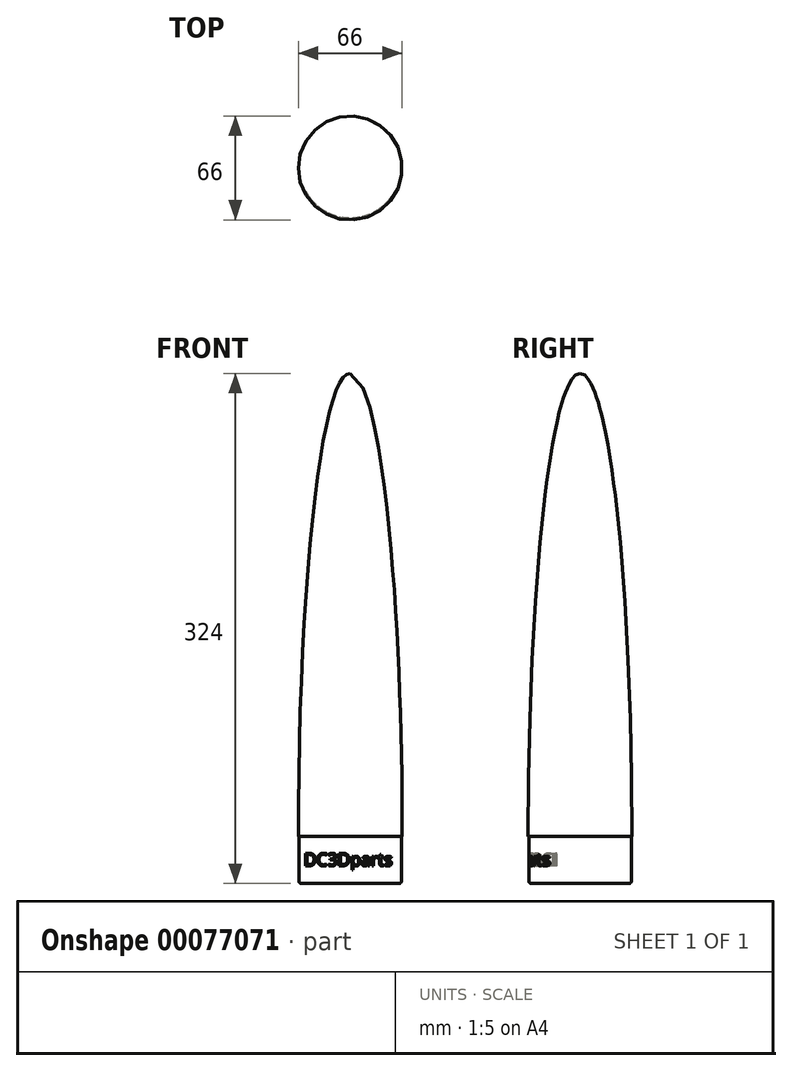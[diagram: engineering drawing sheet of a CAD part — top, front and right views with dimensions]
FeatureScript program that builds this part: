
annotation { "Feature Type Name" : "Feature", "Feature Type Description" : "" }
export const myFeature = defineFeature(function(context is Context, id is Id, definition is map)
    precondition{}
    {
        {
            var Q0;
            Q0=qCreatedBy(makeId("Front.planeOp"),FACE);
            var sketch = newSketch(context, id + "F0", { "sketchPlane" : qUnion([Q0])});
            skEllipticalArc(sketch, "E0", {});
            skLineSegment(sketch, "E1", {"start": v(0, 294) * mm, "end": v(0, -294) * mm, "construction": true});
            skPoint(sketch, "E1.endSnap0", {"position": v(0, 294) * mm});
            skLineSegment(sketch, "E2", {"start": v(-35.36, 0) * mm, "end": v(40.39, 0) * mm, "construction": true});
            skPoint(sketch, "E2.endSnap0", {"position": v(33, 0) * mm});
            skPoint(sketch, "E3.orphan", {"position": v(0, 67.2) * mm});
            skPoint(sketch, "E4.orphan", {"position": v(0, -68.03) * mm});
            skLineSegment(sketch, "E5", {"start": v(-33, 0) * mm, "end": v(-32.55, 0) * mm});
            skLineSegment(sketch, "E6", {"start": v(-32.55, 0) * mm, "end": v(-32.55, -30) * mm});
            skLineSegment(sketch, "E7", {"start": v(-32.55, -30) * mm, "end": v(0, -30) * mm});
            skLineSegment(sketch, "E8", {"start": v(0, -30) * mm, "end": v(0, 294) * mm});
            const initialGuessF0  = {"E0": [0, 0, 0, 1, 0.294, 0.033, 0, 1.5707963267948966]};
            skSetInitialGuess(sketch, initialGuessF0);
            skSolve(sketch);
        }
        {
            var Q0;
            Q0=makeQuery(id+"F0.imprint","IMPRINT",FACE,{"disambiguationData":[TD([[makeQuery(id+"F0.imprint","IMPRINT",EDGE,{"derivedFrom":sQuery(id+"F0.wireOp",EDGE,"E0")}),1.0]])]});
            var Q1;
            Q1=sQuery(id+"F0.wireOp",EDGE,"E1");
            revolve(context, id + "F1", {"entities" : qUnion([Q0]), "axis" : qUnion([Q1]), "revolveType" : RevolveType.FULL});
        }
        {
            var Q0;
            Q0=qCreatedBy(makeId("Front.planeOp"),FACE);
            cPlane(context, id + "F2", {"entities" : qUnion([Q0]), "cplaneType" : CPlaneType.OFFSET, "offset" : 40 * mm, "width" : 150 * mm, "height" : 150 * mm});
        }
        {
            var Q0;
            Q0=qCreatedBy(id+"F2.planeOp",FACE);
            var sketch = newSketch(context, id + "F3", { "sketchPlane" : qUnion([Q0])});
            skText(sketch, "E9", { "text": "DC3Dparts", "fontName": "OpenSans-Regular.ttf"});
            const initialGuessF3  = {"E9": [-0.02955, -0.01876, 1, 0, 0.008]};
            skSetInitialGuess(sketch, initialGuessF3);
            skSolve(sketch);
        }
        {
            var Q0;
            Q0=qCreatedBy(makeId("Front.planeOp"),FACE);
            var sketch = newSketch(context, id + "F4", { "sketchPlane" : qUnion([Q0])});
            skLineSegment(sketch, "E10.bottom", {"start": v(0, -9.12) * mm, "end": v(-32, -9.12) * mm});
            skLineSegment(sketch, "E10.top", {"start": v(0, -47.4) * mm, "end": v(-32, -47.4) * mm});
            skLineSegment(sketch, "E10.left", {"start": v(0, -9.12) * mm, "end": v(0, -47.4) * mm});
            skLineSegment(sketch, "E10.right", {"start": v(-32, -9.12) * mm, "end": v(-32, -47.4) * mm});
            skLineSegment(sketch, "E11.left", {"start": v(0, -47.4) * mm, "end": v(0, -47.4) * mm});
            skLineSegment(sketch, "E11.right", {"start": v(-32, -47.4) * mm, "end": v(-32, -47.4) * mm});
            skLineSegment(sketch, "E12.bottom", {"start": v(-32, -9.12) * mm, "end": v(-58.46, -9.12) * mm});
            skLineSegment(sketch, "E12.top", {"start": v(-32, -52.19) * mm, "end": v(-58.46, -52.19) * mm});
            skLineSegment(sketch, "E12.left", {"start": v(-32, -9.12) * mm, "end": v(-32, -52.19) * mm});
            skLineSegment(sketch, "E12.right", {"start": v(-58.46, -9.12) * mm, "end": v(-58.46, -52.19) * mm});
            skSolve(sketch);
        }
        {
            var Q0;
            Q0 = qSketchRegion(id + "F3", true);
            extrude(context, id + "F5", {"entities" : qUnion([Q0]), "oppositeDirection" : true, "depth" : 38 * mm, "offsetDistance" : 25 * mm});
        }
        {
            var Q0;
            {var subQ0=sQuery(id+"F4.wireOp",EDGE,"E10.bottom");Q0=makeQuery(id+"F4.imprint","IMPRINT",FACE,{"disambiguationData":[TD([[makeQuery(id+"F4.imprint","IMPRINT",EDGE,{"derivedFrom":subQ0}),1.0]])]});}
            var Q1;
            Q1=sQuery(id+"F4.wireOp",EDGE,"E10.left");
            revolve(context, id + "F6", {"entities" : qUnion([Q0]), "axis" : qUnion([Q1]), "revolveType" : RevolveType.FULL});
        }
        {
            var Q0;
            Q0=makeQuery(id+"F6.opRevolve","SWEPT_BODY",BODY,{"disambiguationData":[OSD([sQuery(id+"F4.wireOp",EDGE,"E10.bottom"),sQuery(id+"F4.wireOp",EDGE,"E10.left"),sQuery(id+"F4.wireOp",EDGE,"E10.top"),sQuery(id+"F4.wireOp",EDGE,"E12.left")])]});
            var Q1;
            Q1=makeQuery(id+"F5.opExtrude","SWEPT_BODY",BODY,{"disambiguationData":[OSD([sQuery(id+"F3.wireOp",EDGE,"E9.sketch_text.stroke-0"),sQuery(id+"F3.wireOp",EDGE,"E9.sketch_text.stroke-1"),sQuery(id+"F3.wireOp",EDGE,"E9.sketch_text.stroke-2"),sQuery(id+"F3.wireOp",EDGE,"E9.sketch_text.stroke-3"),sQuery(id+"F3.wireOp",EDGE,"E9.sketch_text.stroke-4"),sQuery(id+"F3.wireOp",EDGE,"E9.sketch_text.stroke-5"),sQuery(id+"F3.wireOp",EDGE,"E9.sketch_text.stroke-6"),sQuery(id+"F3.wireOp",EDGE,"E9.sketch_text.stroke-7"),sQuery(id+"F3.wireOp",EDGE,"E9.sketch_text.stroke-8"),sQuery(id+"F3.wireOp",EDGE,"E9.sketch_text.stroke-9"),sQuery(id+"F3.wireOp",EDGE,"E9.sketch_text.stroke-10"),sQuery(id+"F3.wireOp",EDGE,"E9.sketch_text.stroke-11"),sQuery(id+"F3.wireOp",EDGE,"E9.sketch_text.stroke-12"),sQuery(id+"F3.wireOp",EDGE,"E9.sketch_text.stroke-13")])]});
            var Q2;
            Q2=makeQuery(id+"F5.opExtrude","SWEPT_BODY",BODY,{"disambiguationData":[OSD([sQuery(id+"F3.wireOp",EDGE,"E9.sketch_text.stroke-14"),sQuery(id+"F3.wireOp",EDGE,"E9.sketch_text.stroke-15"),sQuery(id+"F3.wireOp",EDGE,"E9.sketch_text.stroke-16"),sQuery(id+"F3.wireOp",EDGE,"E9.sketch_text.stroke-17"),sQuery(id+"F3.wireOp",EDGE,"E9.sketch_text.stroke-18"),sQuery(id+"F3.wireOp",EDGE,"E9.sketch_text.stroke-19"),sQuery(id+"F3.wireOp",EDGE,"E9.sketch_text.stroke-20"),sQuery(id+"F3.wireOp",EDGE,"E9.sketch_text.stroke-21"),sQuery(id+"F3.wireOp",EDGE,"E9.sketch_text.stroke-22"),sQuery(id+"F3.wireOp",EDGE,"E9.sketch_text.stroke-23"),sQuery(id+"F3.wireOp",EDGE,"E9.sketch_text.stroke-24"),sQuery(id+"F3.wireOp",EDGE,"E9.sketch_text.stroke-25"),sQuery(id+"F3.wireOp",EDGE,"E9.sketch_text.stroke-26"),sQuery(id+"F3.wireOp",EDGE,"E9.sketch_text.stroke-27"),sQuery(id+"F3.wireOp",EDGE,"E9.sketch_text.stroke-28")])]});
            var Q3;
            Q3=makeQuery(id+"F5.opExtrude","SWEPT_BODY",BODY,{"disambiguationData":[OSD([sQuery(id+"F3.wireOp",EDGE,"E9.sketch_text.stroke-29"),sQuery(id+"F3.wireOp",EDGE,"E9.sketch_text.stroke-30"),sQuery(id+"F3.wireOp",EDGE,"E9.sketch_text.stroke-31"),sQuery(id+"F3.wireOp",EDGE,"E9.sketch_text.stroke-32"),sQuery(id+"F3.wireOp",EDGE,"E9.sketch_text.stroke-33"),sQuery(id+"F3.wireOp",EDGE,"E9.sketch_text.stroke-34"),sQuery(id+"F3.wireOp",EDGE,"E9.sketch_text.stroke-35"),sQuery(id+"F3.wireOp",EDGE,"E9.sketch_text.stroke-36"),sQuery(id+"F3.wireOp",EDGE,"E9.sketch_text.stroke-37"),sQuery(id+"F3.wireOp",EDGE,"E9.sketch_text.stroke-38"),sQuery(id+"F3.wireOp",EDGE,"E9.sketch_text.stroke-39"),sQuery(id+"F3.wireOp",EDGE,"E9.sketch_text.stroke-40"),sQuery(id+"F3.wireOp",EDGE,"E9.sketch_text.stroke-41"),sQuery(id+"F3.wireOp",EDGE,"E9.sketch_text.stroke-42"),sQuery(id+"F3.wireOp",EDGE,"E9.sketch_text.stroke-43"),sQuery(id+"F3.wireOp",EDGE,"E9.sketch_text.stroke-44"),sQuery(id+"F3.wireOp",EDGE,"E9.sketch_text.stroke-45"),sQuery(id+"F3.wireOp",EDGE,"E9.sketch_text.stroke-46"),sQuery(id+"F3.wireOp",EDGE,"E9.sketch_text.stroke-47"),sQuery(id+"F3.wireOp",EDGE,"E9.sketch_text.stroke-48"),sQuery(id+"F3.wireOp",EDGE,"E9.sketch_text.stroke-49"),sQuery(id+"F3.wireOp",EDGE,"E9.sketch_text.stroke-50"),sQuery(id+"F3.wireOp",EDGE,"E9.sketch_text.stroke-51"),sQuery(id+"F3.wireOp",EDGE,"E9.sketch_text.stroke-52"),sQuery(id+"F3.wireOp",EDGE,"E9.sketch_text.stroke-53"),sQuery(id+"F3.wireOp",EDGE,"E9.sketch_text.stroke-54"),sQuery(id+"F3.wireOp",EDGE,"E9.sketch_text.stroke-55"),sQuery(id+"F3.wireOp",EDGE,"E9.sketch_text.stroke-56")])]});
            var Q4;
            Q4=makeQuery(id+"F5.opExtrude","SWEPT_BODY",BODY,{"disambiguationData":[OSD([sQuery(id+"F3.wireOp",EDGE,"E9.sketch_text.stroke-57"),sQuery(id+"F3.wireOp",EDGE,"E9.sketch_text.stroke-58"),sQuery(id+"F3.wireOp",EDGE,"E9.sketch_text.stroke-59"),sQuery(id+"F3.wireOp",EDGE,"E9.sketch_text.stroke-60"),sQuery(id+"F3.wireOp",EDGE,"E9.sketch_text.stroke-61"),sQuery(id+"F3.wireOp",EDGE,"E9.sketch_text.stroke-62"),sQuery(id+"F3.wireOp",EDGE,"E9.sketch_text.stroke-63"),sQuery(id+"F3.wireOp",EDGE,"E9.sketch_text.stroke-64"),sQuery(id+"F3.wireOp",EDGE,"E9.sketch_text.stroke-65"),sQuery(id+"F3.wireOp",EDGE,"E9.sketch_text.stroke-66"),sQuery(id+"F3.wireOp",EDGE,"E9.sketch_text.stroke-67"),sQuery(id+"F3.wireOp",EDGE,"E9.sketch_text.stroke-68"),sQuery(id+"F3.wireOp",EDGE,"E9.sketch_text.stroke-69"),sQuery(id+"F3.wireOp",EDGE,"E9.sketch_text.stroke-70")])]});
            var Q5;
            Q5=makeQuery(id+"F5.opExtrude","SWEPT_BODY",BODY,{"disambiguationData":[OSD([sQuery(id+"F3.wireOp",EDGE,"E9.sketch_text.stroke-71"),sQuery(id+"F3.wireOp",EDGE,"E9.sketch_text.stroke-72"),sQuery(id+"F3.wireOp",EDGE,"E9.sketch_text.stroke-73"),sQuery(id+"F3.wireOp",EDGE,"E9.sketch_text.stroke-74"),sQuery(id+"F3.wireOp",EDGE,"E9.sketch_text.stroke-75"),sQuery(id+"F3.wireOp",EDGE,"E9.sketch_text.stroke-76"),sQuery(id+"F3.wireOp",EDGE,"E9.sketch_text.stroke-77"),sQuery(id+"F3.wireOp",EDGE,"E9.sketch_text.stroke-78"),sQuery(id+"F3.wireOp",EDGE,"E9.sketch_text.stroke-79"),sQuery(id+"F3.wireOp",EDGE,"E9.sketch_text.stroke-80"),sQuery(id+"F3.wireOp",EDGE,"E9.sketch_text.stroke-81"),sQuery(id+"F3.wireOp",EDGE,"E9.sketch_text.stroke-82"),sQuery(id+"F3.wireOp",EDGE,"E9.sketch_text.stroke-83"),sQuery(id+"F3.wireOp",EDGE,"E9.sketch_text.stroke-84"),sQuery(id+"F3.wireOp",EDGE,"E9.sketch_text.stroke-85"),sQuery(id+"F3.wireOp",EDGE,"E9.sketch_text.stroke-86"),sQuery(id+"F3.wireOp",EDGE,"E9.sketch_text.stroke-87"),sQuery(id+"F3.wireOp",EDGE,"E9.sketch_text.stroke-88"),sQuery(id+"F3.wireOp",EDGE,"E9.sketch_text.stroke-89"),sQuery(id+"F3.wireOp",EDGE,"E9.sketch_text.stroke-90"),sQuery(id+"F3.wireOp",EDGE,"E9.sketch_text.stroke-91"),sQuery(id+"F3.wireOp",EDGE,"E9.sketch_text.stroke-92"),sQuery(id+"F3.wireOp",EDGE,"E9.sketch_text.stroke-93"),sQuery(id+"F3.wireOp",EDGE,"E9.sketch_text.stroke-94"),sQuery(id+"F3.wireOp",EDGE,"E9.sketch_text.stroke-95")])]});
            var Q6;
            Q6=makeQuery(id+"F5.opExtrude","SWEPT_BODY",BODY,{"disambiguationData":[OSD([sQuery(id+"F3.wireOp",EDGE,"E9.sketch_text.stroke-96"),sQuery(id+"F3.wireOp",EDGE,"E9.sketch_text.stroke-97"),sQuery(id+"F3.wireOp",EDGE,"E9.sketch_text.stroke-98"),sQuery(id+"F3.wireOp",EDGE,"E9.sketch_text.stroke-99"),sQuery(id+"F3.wireOp",EDGE,"E9.sketch_text.stroke-100"),sQuery(id+"F3.wireOp",EDGE,"E9.sketch_text.stroke-101"),sQuery(id+"F3.wireOp",EDGE,"E9.sketch_text.stroke-102"),sQuery(id+"F3.wireOp",EDGE,"E9.sketch_text.stroke-103"),sQuery(id+"F3.wireOp",EDGE,"E9.sketch_text.stroke-104"),sQuery(id+"F3.wireOp",EDGE,"E9.sketch_text.stroke-105"),sQuery(id+"F3.wireOp",EDGE,"E9.sketch_text.stroke-106"),sQuery(id+"F3.wireOp",EDGE,"E9.sketch_text.stroke-107"),sQuery(id+"F3.wireOp",EDGE,"E9.sketch_text.stroke-108"),sQuery(id+"F3.wireOp",EDGE,"E9.sketch_text.stroke-109"),sQuery(id+"F3.wireOp",EDGE,"E9.sketch_text.stroke-110"),sQuery(id+"F3.wireOp",EDGE,"E9.sketch_text.stroke-111"),sQuery(id+"F3.wireOp",EDGE,"E9.sketch_text.stroke-112"),sQuery(id+"F3.wireOp",EDGE,"E9.sketch_text.stroke-113"),sQuery(id+"F3.wireOp",EDGE,"E9.sketch_text.stroke-114"),sQuery(id+"F3.wireOp",EDGE,"E9.sketch_text.stroke-115"),sQuery(id+"F3.wireOp",EDGE,"E9.sketch_text.stroke-116"),sQuery(id+"F3.wireOp",EDGE,"E9.sketch_text.stroke-117"),sQuery(id+"F3.wireOp",EDGE,"E9.sketch_text.stroke-118"),sQuery(id+"F3.wireOp",EDGE,"E9.sketch_text.stroke-119"),sQuery(id+"F3.wireOp",EDGE,"E9.sketch_text.stroke-120"),sQuery(id+"F3.wireOp",EDGE,"E9.sketch_text.stroke-121"),sQuery(id+"F3.wireOp",EDGE,"E9.sketch_text.stroke-122")])]});
            var Q7;
            Q7=makeQuery(id+"F5.opExtrude","SWEPT_BODY",BODY,{"disambiguationData":[OSD([sQuery(id+"F3.wireOp",EDGE,"E9.sketch_text.stroke-123"),sQuery(id+"F3.wireOp",EDGE,"E9.sketch_text.stroke-124"),sQuery(id+"F3.wireOp",EDGE,"E9.sketch_text.stroke-125"),sQuery(id+"F3.wireOp",EDGE,"E9.sketch_text.stroke-126"),sQuery(id+"F3.wireOp",EDGE,"E9.sketch_text.stroke-127"),sQuery(id+"F3.wireOp",EDGE,"E9.sketch_text.stroke-128"),sQuery(id+"F3.wireOp",EDGE,"E9.sketch_text.stroke-129"),sQuery(id+"F3.wireOp",EDGE,"E9.sketch_text.stroke-130"),sQuery(id+"F3.wireOp",EDGE,"E9.sketch_text.stroke-131"),sQuery(id+"F3.wireOp",EDGE,"E9.sketch_text.stroke-132"),sQuery(id+"F3.wireOp",EDGE,"E9.sketch_text.stroke-133"),sQuery(id+"F3.wireOp",EDGE,"E9.sketch_text.stroke-134"),sQuery(id+"F3.wireOp",EDGE,"E9.sketch_text.stroke-135")])]});
            var Q8;
            Q8=makeQuery(id+"F5.opExtrude","SWEPT_BODY",BODY,{"disambiguationData":[OSD([sQuery(id+"F3.wireOp",EDGE,"E9.sketch_text.stroke-136"),sQuery(id+"F3.wireOp",EDGE,"E9.sketch_text.stroke-137"),sQuery(id+"F3.wireOp",EDGE,"E9.sketch_text.stroke-138"),sQuery(id+"F3.wireOp",EDGE,"E9.sketch_text.stroke-139"),sQuery(id+"F3.wireOp",EDGE,"E9.sketch_text.stroke-140"),sQuery(id+"F3.wireOp",EDGE,"E9.sketch_text.stroke-141"),sQuery(id+"F3.wireOp",EDGE,"E9.sketch_text.stroke-142"),sQuery(id+"F3.wireOp",EDGE,"E9.sketch_text.stroke-143"),sQuery(id+"F3.wireOp",EDGE,"E9.sketch_text.stroke-144"),sQuery(id+"F3.wireOp",EDGE,"E9.sketch_text.stroke-145"),sQuery(id+"F3.wireOp",EDGE,"E9.sketch_text.stroke-146"),sQuery(id+"F3.wireOp",EDGE,"E9.sketch_text.stroke-147"),sQuery(id+"F3.wireOp",EDGE,"E9.sketch_text.stroke-148"),sQuery(id+"F3.wireOp",EDGE,"E9.sketch_text.stroke-149"),sQuery(id+"F3.wireOp",EDGE,"E9.sketch_text.stroke-150"),sQuery(id+"F3.wireOp",EDGE,"E9.sketch_text.stroke-151"),sQuery(id+"F3.wireOp",EDGE,"E9.sketch_text.stroke-152"),sQuery(id+"F3.wireOp",EDGE,"E9.sketch_text.stroke-153"),sQuery(id+"F3.wireOp",EDGE,"E9.sketch_text.stroke-154")])]});
            var Q9;
            Q9=makeQuery(id+"F5.opExtrude","SWEPT_BODY",BODY,{"disambiguationData":[OSD([sQuery(id+"F3.wireOp",EDGE,"E9.sketch_text.stroke-155"),sQuery(id+"F3.wireOp",EDGE,"E9.sketch_text.stroke-156"),sQuery(id+"F3.wireOp",EDGE,"E9.sketch_text.stroke-157"),sQuery(id+"F3.wireOp",EDGE,"E9.sketch_text.stroke-158"),sQuery(id+"F3.wireOp",EDGE,"E9.sketch_text.stroke-159"),sQuery(id+"F3.wireOp",EDGE,"E9.sketch_text.stroke-160"),sQuery(id+"F3.wireOp",EDGE,"E9.sketch_text.stroke-161"),sQuery(id+"F3.wireOp",EDGE,"E9.sketch_text.stroke-162"),sQuery(id+"F3.wireOp",EDGE,"E9.sketch_text.stroke-163"),sQuery(id+"F3.wireOp",EDGE,"E9.sketch_text.stroke-164"),sQuery(id+"F3.wireOp",EDGE,"E9.sketch_text.stroke-165"),sQuery(id+"F3.wireOp",EDGE,"E9.sketch_text.stroke-166"),sQuery(id+"F3.wireOp",EDGE,"E9.sketch_text.stroke-167"),sQuery(id+"F3.wireOp",EDGE,"E9.sketch_text.stroke-168"),sQuery(id+"F3.wireOp",EDGE,"E9.sketch_text.stroke-169"),sQuery(id+"F3.wireOp",EDGE,"E9.sketch_text.stroke-170"),sQuery(id+"F3.wireOp",EDGE,"E9.sketch_text.stroke-171"),sQuery(id+"F3.wireOp",EDGE,"E9.sketch_text.stroke-172"),sQuery(id+"F3.wireOp",EDGE,"E9.sketch_text.stroke-173"),sQuery(id+"F3.wireOp",EDGE,"E9.sketch_text.stroke-174"),sQuery(id+"F3.wireOp",EDGE,"E9.sketch_text.stroke-175"),sQuery(id+"F3.wireOp",EDGE,"E9.sketch_text.stroke-176"),sQuery(id+"F3.wireOp",EDGE,"E9.sketch_text.stroke-177"),sQuery(id+"F3.wireOp",EDGE,"E9.sketch_text.stroke-178"),sQuery(id+"F3.wireOp",EDGE,"E9.sketch_text.stroke-179")])]});
            booleanBodies(context, id + "F7", {"operationType" : BooleanOperationType.SUBTRACTION, "tools" : qUnion([Q0]), "targets" : qUnion([Q1, Q2, Q3, Q4, Q5, Q6, Q7, Q8, Q9])});
        }
        {
            var Q0;
            Q0=makeQuery(id+"F5.opExtrude","SWEPT_BODY",BODY,{"disambiguationData":[OSD([sQuery(id+"F3.wireOp",EDGE,"E9.sketch_text.stroke-0"),sQuery(id+"F3.wireOp",EDGE,"E9.sketch_text.stroke-1"),sQuery(id+"F3.wireOp",EDGE,"E9.sketch_text.stroke-2"),sQuery(id+"F3.wireOp",EDGE,"E9.sketch_text.stroke-3"),sQuery(id+"F3.wireOp",EDGE,"E9.sketch_text.stroke-4"),sQuery(id+"F3.wireOp",EDGE,"E9.sketch_text.stroke-5"),sQuery(id+"F3.wireOp",EDGE,"E9.sketch_text.stroke-6"),sQuery(id+"F3.wireOp",EDGE,"E9.sketch_text.stroke-7"),sQuery(id+"F3.wireOp",EDGE,"E9.sketch_text.stroke-8"),sQuery(id+"F3.wireOp",EDGE,"E9.sketch_text.stroke-9"),sQuery(id+"F3.wireOp",EDGE,"E9.sketch_text.stroke-10"),sQuery(id+"F3.wireOp",EDGE,"E9.sketch_text.stroke-11"),sQuery(id+"F3.wireOp",EDGE,"E9.sketch_text.stroke-12"),sQuery(id+"F3.wireOp",EDGE,"E9.sketch_text.stroke-13")])]});
            var Q1;
            Q1=makeQuery(id+"F5.opExtrude","SWEPT_BODY",BODY,{"disambiguationData":[OSD([sQuery(id+"F3.wireOp",EDGE,"E9.sketch_text.stroke-14"),sQuery(id+"F3.wireOp",EDGE,"E9.sketch_text.stroke-15"),sQuery(id+"F3.wireOp",EDGE,"E9.sketch_text.stroke-16"),sQuery(id+"F3.wireOp",EDGE,"E9.sketch_text.stroke-17"),sQuery(id+"F3.wireOp",EDGE,"E9.sketch_text.stroke-18"),sQuery(id+"F3.wireOp",EDGE,"E9.sketch_text.stroke-19"),sQuery(id+"F3.wireOp",EDGE,"E9.sketch_text.stroke-20"),sQuery(id+"F3.wireOp",EDGE,"E9.sketch_text.stroke-21"),sQuery(id+"F3.wireOp",EDGE,"E9.sketch_text.stroke-22"),sQuery(id+"F3.wireOp",EDGE,"E9.sketch_text.stroke-23"),sQuery(id+"F3.wireOp",EDGE,"E9.sketch_text.stroke-24"),sQuery(id+"F3.wireOp",EDGE,"E9.sketch_text.stroke-25"),sQuery(id+"F3.wireOp",EDGE,"E9.sketch_text.stroke-26"),sQuery(id+"F3.wireOp",EDGE,"E9.sketch_text.stroke-27"),sQuery(id+"F3.wireOp",EDGE,"E9.sketch_text.stroke-28")])]});
            var Q2;
            Q2=makeQuery(id+"F5.opExtrude","SWEPT_BODY",BODY,{"disambiguationData":[OSD([sQuery(id+"F3.wireOp",EDGE,"E9.sketch_text.stroke-29"),sQuery(id+"F3.wireOp",EDGE,"E9.sketch_text.stroke-30"),sQuery(id+"F3.wireOp",EDGE,"E9.sketch_text.stroke-31"),sQuery(id+"F3.wireOp",EDGE,"E9.sketch_text.stroke-32"),sQuery(id+"F3.wireOp",EDGE,"E9.sketch_text.stroke-33"),sQuery(id+"F3.wireOp",EDGE,"E9.sketch_text.stroke-34"),sQuery(id+"F3.wireOp",EDGE,"E9.sketch_text.stroke-35"),sQuery(id+"F3.wireOp",EDGE,"E9.sketch_text.stroke-36"),sQuery(id+"F3.wireOp",EDGE,"E9.sketch_text.stroke-37"),sQuery(id+"F3.wireOp",EDGE,"E9.sketch_text.stroke-38"),sQuery(id+"F3.wireOp",EDGE,"E9.sketch_text.stroke-39"),sQuery(id+"F3.wireOp",EDGE,"E9.sketch_text.stroke-40"),sQuery(id+"F3.wireOp",EDGE,"E9.sketch_text.stroke-41"),sQuery(id+"F3.wireOp",EDGE,"E9.sketch_text.stroke-42"),sQuery(id+"F3.wireOp",EDGE,"E9.sketch_text.stroke-43"),sQuery(id+"F3.wireOp",EDGE,"E9.sketch_text.stroke-44"),sQuery(id+"F3.wireOp",EDGE,"E9.sketch_text.stroke-45"),sQuery(id+"F3.wireOp",EDGE,"E9.sketch_text.stroke-46"),sQuery(id+"F3.wireOp",EDGE,"E9.sketch_text.stroke-47"),sQuery(id+"F3.wireOp",EDGE,"E9.sketch_text.stroke-48"),sQuery(id+"F3.wireOp",EDGE,"E9.sketch_text.stroke-49"),sQuery(id+"F3.wireOp",EDGE,"E9.sketch_text.stroke-50"),sQuery(id+"F3.wireOp",EDGE,"E9.sketch_text.stroke-51"),sQuery(id+"F3.wireOp",EDGE,"E9.sketch_text.stroke-52"),sQuery(id+"F3.wireOp",EDGE,"E9.sketch_text.stroke-53"),sQuery(id+"F3.wireOp",EDGE,"E9.sketch_text.stroke-54"),sQuery(id+"F3.wireOp",EDGE,"E9.sketch_text.stroke-55"),sQuery(id+"F3.wireOp",EDGE,"E9.sketch_text.stroke-56")])]});
            var Q3;
            Q3=makeQuery(id+"F5.opExtrude","SWEPT_BODY",BODY,{"disambiguationData":[OSD([sQuery(id+"F3.wireOp",EDGE,"E9.sketch_text.stroke-57"),sQuery(id+"F3.wireOp",EDGE,"E9.sketch_text.stroke-58"),sQuery(id+"F3.wireOp",EDGE,"E9.sketch_text.stroke-59"),sQuery(id+"F3.wireOp",EDGE,"E9.sketch_text.stroke-60"),sQuery(id+"F3.wireOp",EDGE,"E9.sketch_text.stroke-61"),sQuery(id+"F3.wireOp",EDGE,"E9.sketch_text.stroke-62"),sQuery(id+"F3.wireOp",EDGE,"E9.sketch_text.stroke-63"),sQuery(id+"F3.wireOp",EDGE,"E9.sketch_text.stroke-64"),sQuery(id+"F3.wireOp",EDGE,"E9.sketch_text.stroke-65"),sQuery(id+"F3.wireOp",EDGE,"E9.sketch_text.stroke-66"),sQuery(id+"F3.wireOp",EDGE,"E9.sketch_text.stroke-67"),sQuery(id+"F3.wireOp",EDGE,"E9.sketch_text.stroke-68"),sQuery(id+"F3.wireOp",EDGE,"E9.sketch_text.stroke-69"),sQuery(id+"F3.wireOp",EDGE,"E9.sketch_text.stroke-70")])]});
            var Q4;
            Q4=makeQuery(id+"F5.opExtrude","SWEPT_BODY",BODY,{"disambiguationData":[OSD([sQuery(id+"F3.wireOp",EDGE,"E9.sketch_text.stroke-71"),sQuery(id+"F3.wireOp",EDGE,"E9.sketch_text.stroke-72"),sQuery(id+"F3.wireOp",EDGE,"E9.sketch_text.stroke-73"),sQuery(id+"F3.wireOp",EDGE,"E9.sketch_text.stroke-74"),sQuery(id+"F3.wireOp",EDGE,"E9.sketch_text.stroke-75"),sQuery(id+"F3.wireOp",EDGE,"E9.sketch_text.stroke-76"),sQuery(id+"F3.wireOp",EDGE,"E9.sketch_text.stroke-77"),sQuery(id+"F3.wireOp",EDGE,"E9.sketch_text.stroke-78"),sQuery(id+"F3.wireOp",EDGE,"E9.sketch_text.stroke-79"),sQuery(id+"F3.wireOp",EDGE,"E9.sketch_text.stroke-80"),sQuery(id+"F3.wireOp",EDGE,"E9.sketch_text.stroke-81"),sQuery(id+"F3.wireOp",EDGE,"E9.sketch_text.stroke-82"),sQuery(id+"F3.wireOp",EDGE,"E9.sketch_text.stroke-83"),sQuery(id+"F3.wireOp",EDGE,"E9.sketch_text.stroke-84"),sQuery(id+"F3.wireOp",EDGE,"E9.sketch_text.stroke-85"),sQuery(id+"F3.wireOp",EDGE,"E9.sketch_text.stroke-86"),sQuery(id+"F3.wireOp",EDGE,"E9.sketch_text.stroke-87"),sQuery(id+"F3.wireOp",EDGE,"E9.sketch_text.stroke-88"),sQuery(id+"F3.wireOp",EDGE,"E9.sketch_text.stroke-89"),sQuery(id+"F3.wireOp",EDGE,"E9.sketch_text.stroke-90"),sQuery(id+"F3.wireOp",EDGE,"E9.sketch_text.stroke-91"),sQuery(id+"F3.wireOp",EDGE,"E9.sketch_text.stroke-92"),sQuery(id+"F3.wireOp",EDGE,"E9.sketch_text.stroke-93"),sQuery(id+"F3.wireOp",EDGE,"E9.sketch_text.stroke-94"),sQuery(id+"F3.wireOp",EDGE,"E9.sketch_text.stroke-95")])]});
            var Q5;
            Q5=makeQuery(id+"F5.opExtrude","SWEPT_BODY",BODY,{"disambiguationData":[OSD([sQuery(id+"F3.wireOp",EDGE,"E9.sketch_text.stroke-96"),sQuery(id+"F3.wireOp",EDGE,"E9.sketch_text.stroke-97"),sQuery(id+"F3.wireOp",EDGE,"E9.sketch_text.stroke-98"),sQuery(id+"F3.wireOp",EDGE,"E9.sketch_text.stroke-99"),sQuery(id+"F3.wireOp",EDGE,"E9.sketch_text.stroke-100"),sQuery(id+"F3.wireOp",EDGE,"E9.sketch_text.stroke-101"),sQuery(id+"F3.wireOp",EDGE,"E9.sketch_text.stroke-102"),sQuery(id+"F3.wireOp",EDGE,"E9.sketch_text.stroke-103"),sQuery(id+"F3.wireOp",EDGE,"E9.sketch_text.stroke-104"),sQuery(id+"F3.wireOp",EDGE,"E9.sketch_text.stroke-105"),sQuery(id+"F3.wireOp",EDGE,"E9.sketch_text.stroke-106"),sQuery(id+"F3.wireOp",EDGE,"E9.sketch_text.stroke-107"),sQuery(id+"F3.wireOp",EDGE,"E9.sketch_text.stroke-108"),sQuery(id+"F3.wireOp",EDGE,"E9.sketch_text.stroke-109"),sQuery(id+"F3.wireOp",EDGE,"E9.sketch_text.stroke-110"),sQuery(id+"F3.wireOp",EDGE,"E9.sketch_text.stroke-111"),sQuery(id+"F3.wireOp",EDGE,"E9.sketch_text.stroke-112"),sQuery(id+"F3.wireOp",EDGE,"E9.sketch_text.stroke-113"),sQuery(id+"F3.wireOp",EDGE,"E9.sketch_text.stroke-114"),sQuery(id+"F3.wireOp",EDGE,"E9.sketch_text.stroke-115"),sQuery(id+"F3.wireOp",EDGE,"E9.sketch_text.stroke-116"),sQuery(id+"F3.wireOp",EDGE,"E9.sketch_text.stroke-117"),sQuery(id+"F3.wireOp",EDGE,"E9.sketch_text.stroke-118"),sQuery(id+"F3.wireOp",EDGE,"E9.sketch_text.stroke-119"),sQuery(id+"F3.wireOp",EDGE,"E9.sketch_text.stroke-120"),sQuery(id+"F3.wireOp",EDGE,"E9.sketch_text.stroke-121"),sQuery(id+"F3.wireOp",EDGE,"E9.sketch_text.stroke-122")])]});
            var Q6;
            Q6=makeQuery(id+"F5.opExtrude","SWEPT_BODY",BODY,{"disambiguationData":[OSD([sQuery(id+"F3.wireOp",EDGE,"E9.sketch_text.stroke-123"),sQuery(id+"F3.wireOp",EDGE,"E9.sketch_text.stroke-124"),sQuery(id+"F3.wireOp",EDGE,"E9.sketch_text.stroke-125"),sQuery(id+"F3.wireOp",EDGE,"E9.sketch_text.stroke-126"),sQuery(id+"F3.wireOp",EDGE,"E9.sketch_text.stroke-127"),sQuery(id+"F3.wireOp",EDGE,"E9.sketch_text.stroke-128"),sQuery(id+"F3.wireOp",EDGE,"E9.sketch_text.stroke-129"),sQuery(id+"F3.wireOp",EDGE,"E9.sketch_text.stroke-130"),sQuery(id+"F3.wireOp",EDGE,"E9.sketch_text.stroke-131"),sQuery(id+"F3.wireOp",EDGE,"E9.sketch_text.stroke-132"),sQuery(id+"F3.wireOp",EDGE,"E9.sketch_text.stroke-133"),sQuery(id+"F3.wireOp",EDGE,"E9.sketch_text.stroke-134"),sQuery(id+"F3.wireOp",EDGE,"E9.sketch_text.stroke-135")])]});
            var Q7;
            Q7=makeQuery(id+"F5.opExtrude","SWEPT_BODY",BODY,{"disambiguationData":[OSD([sQuery(id+"F3.wireOp",EDGE,"E9.sketch_text.stroke-155"),sQuery(id+"F3.wireOp",EDGE,"E9.sketch_text.stroke-156"),sQuery(id+"F3.wireOp",EDGE,"E9.sketch_text.stroke-157"),sQuery(id+"F3.wireOp",EDGE,"E9.sketch_text.stroke-158"),sQuery(id+"F3.wireOp",EDGE,"E9.sketch_text.stroke-159"),sQuery(id+"F3.wireOp",EDGE,"E9.sketch_text.stroke-160"),sQuery(id+"F3.wireOp",EDGE,"E9.sketch_text.stroke-161"),sQuery(id+"F3.wireOp",EDGE,"E9.sketch_text.stroke-162"),sQuery(id+"F3.wireOp",EDGE,"E9.sketch_text.stroke-163"),sQuery(id+"F3.wireOp",EDGE,"E9.sketch_text.stroke-164"),sQuery(id+"F3.wireOp",EDGE,"E9.sketch_text.stroke-165"),sQuery(id+"F3.wireOp",EDGE,"E9.sketch_text.stroke-166"),sQuery(id+"F3.wireOp",EDGE,"E9.sketch_text.stroke-167"),sQuery(id+"F3.wireOp",EDGE,"E9.sketch_text.stroke-168"),sQuery(id+"F3.wireOp",EDGE,"E9.sketch_text.stroke-169"),sQuery(id+"F3.wireOp",EDGE,"E9.sketch_text.stroke-170"),sQuery(id+"F3.wireOp",EDGE,"E9.sketch_text.stroke-171"),sQuery(id+"F3.wireOp",EDGE,"E9.sketch_text.stroke-172"),sQuery(id+"F3.wireOp",EDGE,"E9.sketch_text.stroke-173"),sQuery(id+"F3.wireOp",EDGE,"E9.sketch_text.stroke-174"),sQuery(id+"F3.wireOp",EDGE,"E9.sketch_text.stroke-175"),sQuery(id+"F3.wireOp",EDGE,"E9.sketch_text.stroke-176"),sQuery(id+"F3.wireOp",EDGE,"E9.sketch_text.stroke-177"),sQuery(id+"F3.wireOp",EDGE,"E9.sketch_text.stroke-178"),sQuery(id+"F3.wireOp",EDGE,"E9.sketch_text.stroke-179")])]});
            var Q8;
            Q8=makeQuery(id+"F5.opExtrude","SWEPT_BODY",BODY,{"disambiguationData":[OSD([sQuery(id+"F3.wireOp",EDGE,"E9.sketch_text.stroke-136"),sQuery(id+"F3.wireOp",EDGE,"E9.sketch_text.stroke-137"),sQuery(id+"F3.wireOp",EDGE,"E9.sketch_text.stroke-138"),sQuery(id+"F3.wireOp",EDGE,"E9.sketch_text.stroke-139"),sQuery(id+"F3.wireOp",EDGE,"E9.sketch_text.stroke-140"),sQuery(id+"F3.wireOp",EDGE,"E9.sketch_text.stroke-141"),sQuery(id+"F3.wireOp",EDGE,"E9.sketch_text.stroke-142"),sQuery(id+"F3.wireOp",EDGE,"E9.sketch_text.stroke-143"),sQuery(id+"F3.wireOp",EDGE,"E9.sketch_text.stroke-144"),sQuery(id+"F3.wireOp",EDGE,"E9.sketch_text.stroke-145"),sQuery(id+"F3.wireOp",EDGE,"E9.sketch_text.stroke-146"),sQuery(id+"F3.wireOp",EDGE,"E9.sketch_text.stroke-147"),sQuery(id+"F3.wireOp",EDGE,"E9.sketch_text.stroke-148"),sQuery(id+"F3.wireOp",EDGE,"E9.sketch_text.stroke-149"),sQuery(id+"F3.wireOp",EDGE,"E9.sketch_text.stroke-150"),sQuery(id+"F3.wireOp",EDGE,"E9.sketch_text.stroke-151"),sQuery(id+"F3.wireOp",EDGE,"E9.sketch_text.stroke-152"),sQuery(id+"F3.wireOp",EDGE,"E9.sketch_text.stroke-153"),sQuery(id+"F3.wireOp",EDGE,"E9.sketch_text.stroke-154")])]});
            var Q9;
            Q9=makeQuery(id+"F1.opRevolve","SWEPT_BODY",BODY,{"disambiguationData":[OSD([sQuery(id+"F0.wireOp",EDGE,"E0"),sQuery(id+"F0.wireOp",EDGE,"E5"),sQuery(id+"F0.wireOp",EDGE,"E6"),sQuery(id+"F0.wireOp",EDGE,"E7"),sQuery(id+"F0.wireOp",EDGE,"E8")])]});
            booleanBodies(context, id + "F8", {"operationType" : BooleanOperationType.SUBTRACTION, "tools" : qUnion([Q0, Q1, Q2, Q3, Q4, Q5, Q6, Q7, Q8]), "targets" : qUnion([Q9])});
        }
        {
            var Q0;
            Q0=makeQuery(id+"F1.opRevolve","SWEPT_EDGE",EDGE,{"disambiguationData":[OSD([sQuery(id+"F0.wireOp",EDGE,"E6"),sQuery(id+"F0.wireOp",EDGE,"E7")])]});
            fillet(context, id + "F9", {"entities" : qUnion([Q0]), "radius" : 1.5 * mm, "tangentPropagation" : true, "allowEdgeOverflow" : false});
        }
    });
